# Revit family: Faucet-Single_Control-American_Standard-Reliant_3-738504X_Series
name_source: partatom
category: Plumbing Fixtures
units: mm (PartAtom-declared; Revit-internal decimal feet)

## family parameters
Always vertical = No
Cut with Voids When Loaded = No
OmniClass Number = 23.45.55.14
OmniClass Title = Single Faucets
Part Type = Normal
Room Calculation Point = No
Round Connector Dimension = Use Diameter
Shared = Yes
Work Plane-Based = Yes

## types (2) — shared parameters
ADA Compliant = Yes
Assembly Code = D2020300
CEC Compliant = Yes
CW Connection = No
CWFU = 1.5
Compliance Certifications = These products meet or exceed the following codes and standards: ANSI A117.1,ASME A112.18.1,NSF 61/Section 9 and Annex G,CSA B125.1
Default Elevation = 0"
Description = Reliant 3® 4-Inch Centerset Single-Handle Bathroom Faucet 1.2 gpm/4.5 L/min With Lever Handle
Flow Rate = 1.2 gpm (4.5 L/min.)
HW Connection = No
HWFU = 1.5
Height = 5 5/8"
Installation Type = Deck Mounted
LH - Extra long Handle = No
Length = 4 7/8"
Manufacturer = American Standard
Pop Up Drain Depth = 3"
Pop Up Drain Width = 3"
Product Documentation Link = https://americanstandard.box.com
Product Page URL = https://www.americanstandard-us.com
RB- Indexed Metal Lever Handle (Red/Blue) = Yes
Revised Date = 09/16/2022
Tempered Water Connection = Yes
Tempered Water Connection Diameter = 3/8"
URL = http://www.americanstandard-us.com
Vent Connection = No
WFU = 2
Waste Connection = No
Width = 6 1/16"

## per-type parameters (varying)
| type | CalGreen Compliant | Finish | Material | Pop-up drain |
| 7385045.295 | Yes | Brass-American Standard-295-Satin Nickel | Brass-American Standard-295-Satin Nickel | Yes |
| 7385047.002 | No | Brass-American Standard-002-Polished Chrome | Brass-American Standard-002-Polished Chrome | No |

note: column(s) folded — value = type name in every type: Model

## geometry (parser evidence)
native form markers: Sweep x5
no freeform markers — native parametric forms only
